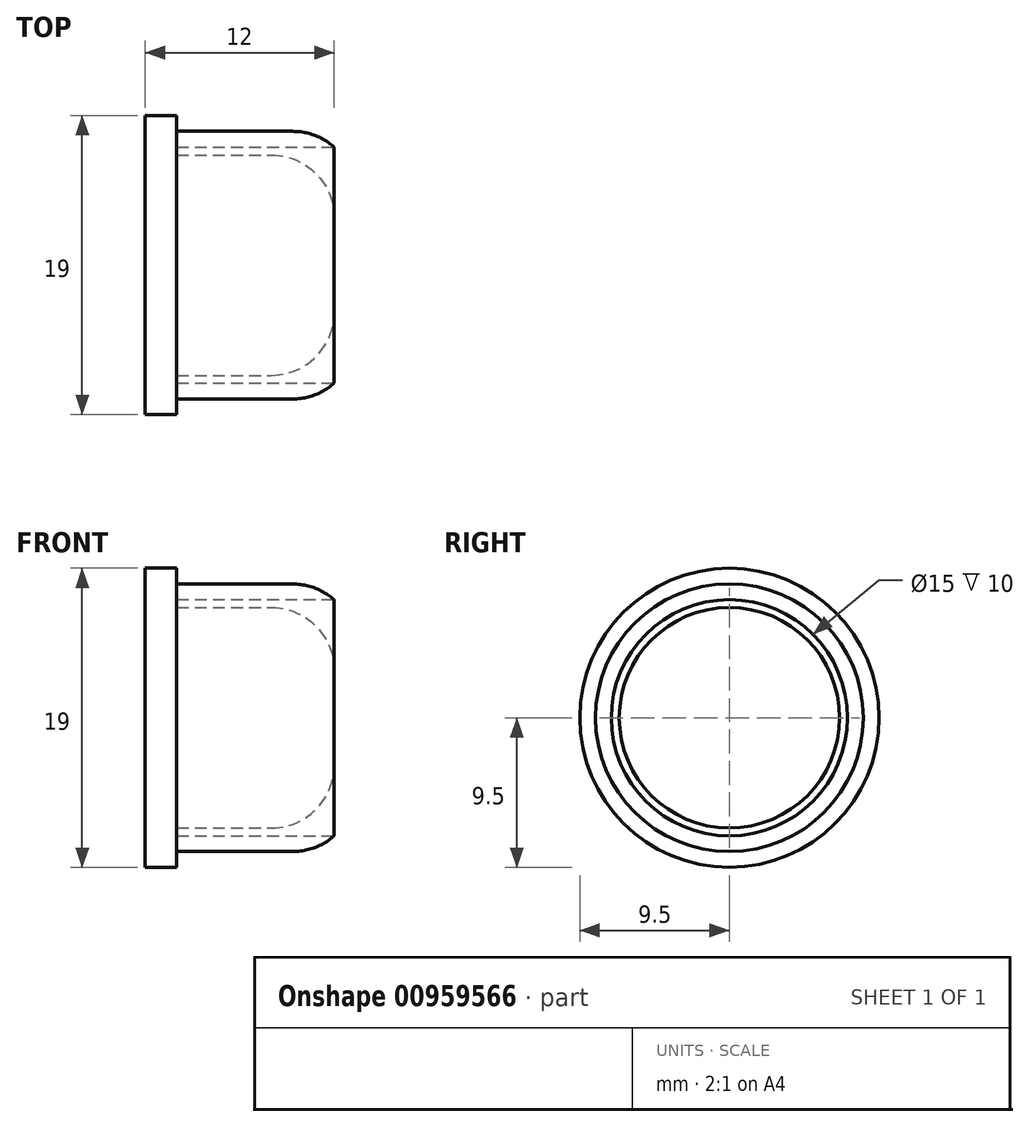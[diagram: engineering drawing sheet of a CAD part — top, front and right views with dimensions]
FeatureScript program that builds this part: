
annotation { "Feature Type Name" : "Feature", "Feature Type Description" : "" }
export const myFeature = defineFeature(function(context is Context, id is Id, definition is map)
    precondition{}
    {
        {
            var Q0;
            Q0=qCreatedBy(makeId("Right.planeOp"),FACE);
            var sketch = newSketch(context, id + "F0", { "sketchPlane" : qUnion([Q0])});
            skCircle(sketch, "E0", {"center": v(0, 0) * mm, "radius": 9.5 * mm});
            skSolve(sketch);
        }
        {
            var Q0;
            Q0 = qSketchRegion(id + "F0", true);
            extrude(context, id + "F1", {"entities" : qUnion([Q0]), "depth" : 2 * mm, "offsetDistance" : 25 * mm});
        }
        {
            var Q0;
            Q0=makeQuery(id+"F1.opExtrude","CAP_FACE",FACE,{"disambiguationData":[OSD([sQuery(id+"F0.wireOp",EDGE,"E0")])],"isStart":false});
            var sketch = newSketch(context, id + "F2", { "sketchPlane" : qUnion([Q0])});
            skCircle(sketch, "E1", {"center": v(0, 0) * mm, "radius": 8.5 * mm});
            skSolve(sketch);
        }
        {
            var Q0;
            Q0 = qSketchRegion(id + "F2", true);
            extrude(context, id + "F3", {"entities" : qUnion([Q0]), "operationType" : NewBodyOperationType.ADD, "depth" : 10 * mm, "offsetDistance" : 25 * mm});
        }
        {
            var Q0;
            Q0=makeQuery(id+"F3.opExtrude","CAP_FACE",FACE,{"disambiguationData":[OSD([sQuery(id+"F2.wireOp",EDGE,"E1")])],"isStart":false});
            var sketch = newSketch(context, id + "F4", { "sketchPlane" : qUnion([Q0])});
            skCircle(sketch, "E2", {"center": v(0, 0) * mm, "radius": 7.5 * mm});
            skCircle(sketch, "E3", {"center": v(0, 0) * mm, "radius": 7 * mm});
            skSolve(sketch);
        }
        {
            var Q0;
            Q0=makeQuery(id+"F4.imprint","IMPRINT",FACE,{"disambiguationData":[TD([[makeQuery(id+"F4.imprint","IMPRINT",EDGE,{"derivedFrom":sQuery(id+"F4.wireOp",EDGE,"E2")}),1.0]])]});
            extrude(context, id + "F5", {"entities" : qUnion([Q0]), "operationType" : NewBodyOperationType.REMOVE, "oppositeDirection" : true, "depth" : 10 * mm, "offsetDistance" : 25 * mm});
        }
        {
            var Q0;
            Q0=makeQuery(id+"F5.boolean.opBoolean","COPY",EDGE,{"derivedFrom":makeQuery(id+"F5.opExtrude","CAP_EDGE",EDGE,{"disambiguationData":[OSD([sQuery(id+"F4.wireOp",EDGE,"E3")])],"isStart":true})});
            var Q1;
            Q1=makeQuery(id+"F3.opExtrude","CAP_EDGE",EDGE,{"disambiguationData":[OSD([sQuery(id+"F2.wireOp",EDGE,"E1")])],"isStart":false});
            fillet(context, id + "F6", {"entities" : qUnion([Q0, Q1]), "radius" : 4 * mm, "tangentPropagation" : true, "allowEdgeOverflow" : false});
        }
    });
